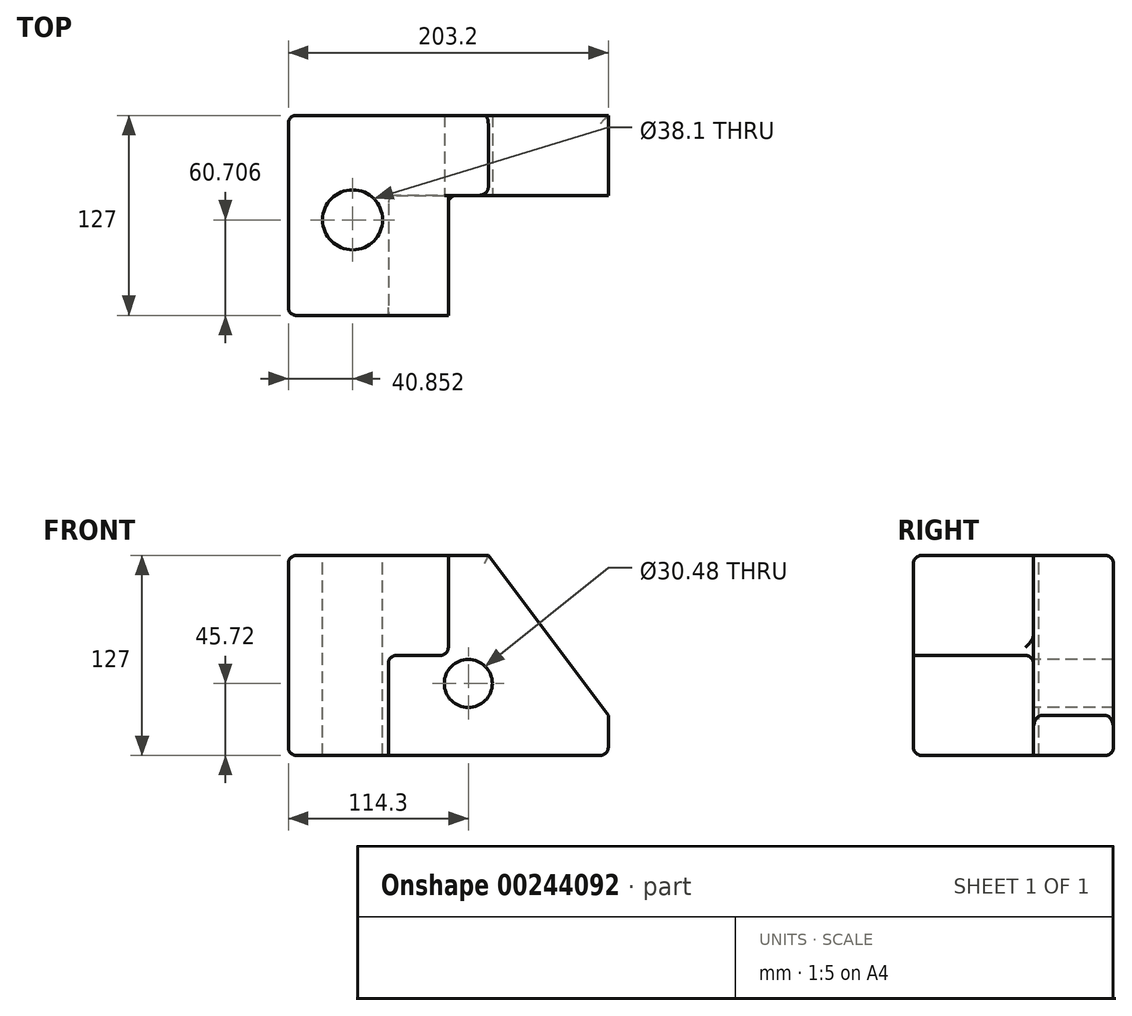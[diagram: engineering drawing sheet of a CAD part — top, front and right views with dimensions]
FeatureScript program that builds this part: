
annotation { "Feature Type Name" : "Feature", "Feature Type Description" : "" }
export const myFeature = defineFeature(function(context is Context, id is Id, definition is map)
    precondition{}
    {
        {
            var Q0;
            Q0=qCreatedBy(makeId("Front.planeOp"),FACE);
            var sketch = newSketch(context, id + "F0", { "sketchPlane" : qUnion([Q0])});
            skLineSegment(sketch, "E0.bottom", {"start": v(101.6, 63.5) * mm, "end": v(-101.6, 63.5) * mm});
            skLineSegment(sketch, "E0.top", {"start": v(101.6, -63.5) * mm, "end": v(-101.6, -63.5) * mm});
            skLineSegment(sketch, "E0.left", {"start": v(101.6, 63.5) * mm, "end": v(101.6, -63.5) * mm});
            skLineSegment(sketch, "E0.right", {"start": v(-101.6, 63.5) * mm, "end": v(-101.6, -63.5) * mm});
            skPoint(sketch, "E0.middle", {"position": v(0, 0) * mm});
            skLineSegment(sketch, "E1", {"start": v(-38.1, -63.5) * mm, "end": v(-38.1, 0) * mm});
            skLineSegment(sketch, "E2", {"start": v(-38.1, 0) * mm, "end": v(0, 0) * mm});
            skLineSegment(sketch, "E3", {"start": v(0, 0) * mm, "end": v(0, 63.5) * mm});
            skSolve(sketch);
        }
        {
            var Q0;
            {var subQ1=sQuery(id+"F0.wireOp",EDGE,"E0.left");Q0=makeQuery(id+"F0.imprint","IMPRINT",FACE,{"disambiguationData":[TD([[makeQuery(id+"F0.imprint","IMPRINT",EDGE,{"derivedFrom":subQ1}),-1.0]])]});}
            var Q1;
            {var subQ1=sQuery(id+"F0.wireOp",EDGE,"E0.right");Q1=makeQuery(id+"F0.imprint","IMPRINT",FACE,{"disambiguationData":[TD([[makeQuery(id+"F0.imprint","IMPRINT",EDGE,{"derivedFrom":subQ1}),1.0]])]});}
            extrude(context, id + "F1", {"entities" : qUnion([Q0, Q1]), "depth" : 127 * mm});
        }
        {
            var Q0;
            Q0=makeQuery(id+"F1.opExtrude","CAP_FACE",FACE,{"disambiguationData":[OSD([sQuery(id+"F0.wireOp",EDGE,"E0.bottom"),sQuery(id+"F0.wireOp",EDGE,"E0.top"),sQuery(id+"F0.wireOp",EDGE,"E0.left"),sQuery(id+"F0.wireOp",EDGE,"E0.right")])],"isStart":false});
            var sketch = newSketch(context, id + "F2", { "sketchPlane" : qUnion([Q0])});
            skLineSegment(sketch, "E4", {"start": v(-101.6, -63.5) * mm, "end": v(-38.1, -63.5) * mm});
            skLineSegment(sketch, "E5", {"start": v(-38.1, -63.5) * mm, "end": v(-38.1, 0) * mm});
            skLineSegment(sketch, "E6", {"start": v(-38.1, 0) * mm, "end": v(0, 0) * mm});
            skLineSegment(sketch, "E7", {"start": v(0, 0) * mm, "end": v(0, 63.5) * mm});
            skSolve(sketch);
        }
        {
            var Q0;
            {var subQ2=sQuery(id+"F2.wireOp",EDGE,"E5");Q0=makeQuery(id+"F2.imprint","IMPRINT",FACE,{"disambiguationData":[TD([[makeQuery(id+"F2.imprint","IMPRINT",EDGE,{"derivedFrom":subQ2}),-1.0]])]});}
            extrude(context, id + "F3", {"entities" : qUnion([Q0]), "operationType" : NewBodyOperationType.REMOVE, "oppositeDirection" : true, "depth" : 76.2 * mm});
        }
        {
            var Q0;
            Q0=makeQuery(id+"F1.opExtrude","SWEPT_EDGE",EDGE,{"disambiguationData":[OSD([sQuery(id+"F0.wireOp",EDGE,"E0.bottom"),sQuery(id+"F0.wireOp",EDGE,"E0.left")])]});
            chamfer(context, id + "F4", {"entities" : qUnion([Q0]), "chamferType" : ChamferType.TWO_OFFSETS, "width1" : 76.2 * mm, "oppositeDirection" : false, "width2" : 101.6 * mm, "tangentPropagation" : true});
        }
        {
            var Q0;
            {var subQ0=sQuery(id+"F0.wireOp",EDGE,"E0.left");var subQ1=sQuery(id+"F0.wireOp",EDGE,"E0.bottom");Q0=makeQuery(id+"F4.opChamfer","BLEND_EDGE",EDGE,{"blendedFrom":[makeQuery(id+"F1.opExtrude","SWEPT_EDGE",EDGE,{"disambiguationData":[OSD([subQ1,subQ0])]}),makeQuery(id+"F3.boolean.opBoolean","COPY",FACE,{"derivedFrom":makeQuery(id+"F3.opExtrude","CAP_FACE",FACE,{"disambiguationData":[OSD([subQ1,sQuery(id+"F0.wireOp",EDGE,"E0.top"),subQ0,sQuery(id+"F2.wireOp",EDGE,"E5"),sQuery(id+"F2.wireOp",EDGE,"E6"),sQuery(id+"F2.wireOp",EDGE,"E7")])],"isStart":false})})],"blendedInto":[makeQuery(id+"F3.boolean.opBoolean","COPY",FACE,{"derivedFrom":makeQuery(id+"F3.opExtrude","CAP_FACE",FACE,{"disambiguationData":[OSD([subQ1,sQuery(id+"F0.wireOp",EDGE,"E0.top"),subQ0,sQuery(id+"F2.wireOp",EDGE,"E5"),sQuery(id+"F2.wireOp",EDGE,"E6"),sQuery(id+"F2.wireOp",EDGE,"E7")])],"isStart":false})})]});}
            var Q1;
            {var subQ0=sQuery(id+"F0.wireOp",EDGE,"E0.left");var subQ1=sQuery(id+"F0.wireOp",EDGE,"E0.bottom");Q1=makeQuery(id+"F4.opChamfer","BLEND_EDGE",EDGE,{"blendedFrom":[makeQuery(id+"F1.opExtrude","SWEPT_EDGE",EDGE,{"disambiguationData":[OSD([subQ1,subQ0])]}),makeQuery(id+"F1.opExtrude","CAP_FACE",FACE,{"disambiguationData":[OSD([subQ1,sQuery(id+"F0.wireOp",EDGE,"E0.top"),subQ0,sQuery(id+"F0.wireOp",EDGE,"E0.right")])],"isStart":true})],"blendedInto":[makeQuery(id+"F1.opExtrude","CAP_FACE",FACE,{"disambiguationData":[OSD([subQ1,sQuery(id+"F0.wireOp",EDGE,"E0.top"),subQ0,sQuery(id+"F0.wireOp",EDGE,"E0.right")])],"isStart":true})]});}
            var Q2;
            Q2=makeQuery(id+"F3.boolean.opBoolean","COPY",EDGE,{"derivedFrom":makeQuery(id+"F3.opExtrude","CAP_EDGE",EDGE,{"disambiguationData":[OSD([sQuery(id+"F0.wireOp",EDGE,"E0.bottom")])],"isStart":false})});
            var Q3;
            Q3=makeQuery(id+"F3.boolean.opBoolean","COPY",EDGE,{"derivedFrom":makeQuery(id+"F3.opExtrude","SWEPT_EDGE",EDGE,{"disambiguationData":[OSD([sQuery(id+"F0.wireOp",EDGE,"E0.bottom"),sQuery(id+"F2.wireOp",EDGE,"E7")])]})});
            var Q4;
            Q4=makeQuery(id+"F1.opExtrude","CAP_EDGE",EDGE,{"disambiguationData":[OSD([sQuery(id+"F0.wireOp",EDGE,"E0.bottom")])],"isStart":false});
            var Q5;
            Q5=makeQuery(id+"F3.boolean.opBoolean","COPY",EDGE,{"derivedFrom":makeQuery(id+"F3.opExtrude","CAP_EDGE",EDGE,{"disambiguationData":[OSD([sQuery(id+"F2.wireOp",EDGE,"E7")])],"isStart":true})});
            var Q6;
            Q6=makeQuery(id+"F3.boolean.opBoolean","COPY",EDGE,{"derivedFrom":makeQuery(id+"F3.opExtrude","SWEPT_EDGE",EDGE,{"disambiguationData":[OSD([sQuery(id+"F2.wireOp",EDGE,"E6"),sQuery(id+"F2.wireOp",EDGE,"E7")])]})});
            var Q7;
            Q7=makeQuery(id+"F3.boolean.opBoolean","COPY",EDGE,{"derivedFrom":makeQuery(id+"F3.opExtrude","CAP_EDGE",EDGE,{"disambiguationData":[OSD([sQuery(id+"F0.wireOp",EDGE,"E0.top")])],"isStart":false})});
            var Q8;
            Q8=makeQuery(id+"F3.boolean.opBoolean","COPY",EDGE,{"derivedFrom":makeQuery(id+"F3.opExtrude","CAP_EDGE",EDGE,{"disambiguationData":[OSD([sQuery(id+"F0.wireOp",EDGE,"E0.left")])],"isStart":false})});
            var Q9;
            Q9=makeQuery(id+"F1.opExtrude","SWEPT_EDGE",EDGE,{"disambiguationData":[OSD([sQuery(id+"F0.wireOp",EDGE,"E0.top"),sQuery(id+"F0.wireOp",EDGE,"E0.left")])]});
            var Q10;
            Q10=makeQuery(id+"F1.opExtrude","CAP_EDGE",EDGE,{"disambiguationData":[OSD([sQuery(id+"F0.wireOp",EDGE,"E0.right")])],"isStart":false});
            var Q11;
            Q11=makeQuery(id+"F1.opExtrude","CAP_EDGE",EDGE,{"disambiguationData":[OSD([sQuery(id+"F0.wireOp",EDGE,"E0.top")])],"isStart":false});
            var Q12;
            Q12=makeQuery(id+"F1.opExtrude","CAP_EDGE",EDGE,{"disambiguationData":[OSD([sQuery(id+"F0.wireOp",EDGE,"E0.bottom")])],"isStart":true});
            var Q13;
            Q13=makeQuery(id+"F1.opExtrude","CAP_EDGE",EDGE,{"disambiguationData":[OSD([sQuery(id+"F0.wireOp",EDGE,"E0.right")])],"isStart":true});
            var Q14;
            Q14=makeQuery(id+"F1.opExtrude","CAP_EDGE",EDGE,{"disambiguationData":[OSD([sQuery(id+"F0.wireOp",EDGE,"E0.top")])],"isStart":true});
            var Q15;
            Q15=makeQuery(id+"F1.opExtrude","SWEPT_EDGE",EDGE,{"disambiguationData":[OSD([sQuery(id+"F0.wireOp",EDGE,"E0.top"),sQuery(id+"F0.wireOp",EDGE,"E0.right")])]});
            var Q16;
            Q16=makeQuery(id+"F3.boolean.opBoolean","COPY",EDGE,{"derivedFrom":makeQuery(id+"F3.opExtrude","SWEPT_EDGE",EDGE,{"disambiguationData":[OSD([sQuery(id+"F0.wireOp",EDGE,"E0.top"),sQuery(id+"F2.wireOp",EDGE,"E4"),sQuery(id+"F2.wireOp",EDGE,"E5")])]})});
            var Q17;
            Q17=makeQuery(id+"F1.opExtrude","SWEPT_EDGE",EDGE,{"disambiguationData":[OSD([sQuery(id+"F0.wireOp",EDGE,"E0.bottom"),sQuery(id+"F0.wireOp",EDGE,"E0.right")])]});
            var Q18;
            Q18=makeQuery(id+"F3.boolean.opBoolean","COPY",EDGE,{"derivedFrom":makeQuery(id+"F3.opExtrude","CAP_EDGE",EDGE,{"disambiguationData":[OSD([sQuery(id+"F2.wireOp",EDGE,"E5")])],"isStart":true})});
            var Q19;
            Q19=makeQuery(id+"F3.boolean.opBoolean","COPY",EDGE,{"derivedFrom":makeQuery(id+"F3.opExtrude","CAP_EDGE",EDGE,{"disambiguationData":[OSD([sQuery(id+"F2.wireOp",EDGE,"E6")])],"isStart":true})});
            var Q20;
            Q20=makeQuery(id+"F3.boolean.opBoolean","COPY",EDGE,{"derivedFrom":makeQuery(id+"F3.opExtrude","SWEPT_EDGE",EDGE,{"disambiguationData":[OSD([sQuery(id+"F2.wireOp",EDGE,"E5"),sQuery(id+"F2.wireOp",EDGE,"E6")])]})});
            var Q21;
            Q21=makeQuery(id+"F3.boolean.opBoolean","COPY",EDGE,{"derivedFrom":makeQuery(id+"F3.opExtrude","CAP_EDGE",EDGE,{"disambiguationData":[OSD([sQuery(id+"F2.wireOp",EDGE,"E6")])],"isStart":false})});
            var Q22;
            Q22=makeQuery(id+"F3.boolean.opBoolean","COPY",EDGE,{"derivedFrom":makeQuery(id+"F3.opExtrude","CAP_EDGE",EDGE,{"disambiguationData":[OSD([sQuery(id+"F2.wireOp",EDGE,"E5")])],"isStart":false})});
            fillet(context, id + "F5", {"entities" : qUnion([Q0, Q1, Q2, Q3, Q4, Q5, Q6, Q7, Q8, Q9, Q10, Q11, Q12, Q13, Q14, Q15, Q16, Q17, Q18, Q19, Q20, Q21, Q22]), "radius" : 5.08 * mm, "tangentPropagation" : true, "allowEdgeOverflow" : false});
        }
        {
            var Q0;
            Q0=makeQuery(id+"F3.boolean.opBoolean","COPY",FACE,{"derivedFrom":makeQuery(id+"F3.opExtrude","CAP_FACE",FACE,{"disambiguationData":[OSD([sQuery(id+"F0.wireOp",EDGE,"E0.bottom"),sQuery(id+"F0.wireOp",EDGE,"E0.top"),sQuery(id+"F0.wireOp",EDGE,"E0.left"),sQuery(id+"F2.wireOp",EDGE,"E5"),sQuery(id+"F2.wireOp",EDGE,"E6"),sQuery(id+"F2.wireOp",EDGE,"E7")])],"isStart":false})});
            var sketch = newSketch(context, id + "F6", { "sketchPlane" : qUnion([Q0])});
            skCircle(sketch, "E8", {"center": v(12.7, -17.78) * mm, "radius": 15.24 * mm});
            skSolve(sketch);
        }
        {
            var Q0;
            Q0=makeQuery(id+"F6.imprint","IMPRINT",FACE,{"disambiguationData":[TD([[makeQuery(id+"F6.imprint","IMPRINT",EDGE,{"derivedFrom":sQuery(id+"F6.wireOp",EDGE,"E8")}),1.0]])]});
            var Q1;
            Q1=makeQuery(id+"F1.opExtrude","CAP_FACE",FACE,{"disambiguationData":[OSD([sQuery(id+"F0.wireOp",EDGE,"E0.bottom"),sQuery(id+"F0.wireOp",EDGE,"E0.top"),sQuery(id+"F0.wireOp",EDGE,"E0.left"),sQuery(id+"F0.wireOp",EDGE,"E0.right")])],"isStart":true});
            extrude(context, id + "F7", {"entities" : qUnion([Q0]), "operationType" : NewBodyOperationType.REMOVE, "endBound" : BoundingType.UP_TO_SURFACE, "oppositeDirection" : true, "endBoundEntityFace" : qUnion([Q1]), "depth" : 25.4 * mm});
        }
        {
            var Q0;
            Q0=makeQuery(id+"F1.opExtrude","SWEPT_FACE",FACE,{"disambiguationData":[OSD([sQuery(id+"F0.wireOp",EDGE,"E0.bottom")])]});
            var sketch = newSketch(context, id + "F8", { "sketchPlane" : qUnion([Q0])});
            skCircle(sketch, "E9", {"center": v(-60.75, -66.3) * mm, "radius": 19.05 * mm});
            skSolve(sketch);
        }
        {
            var Q0;
            Q0=makeQuery(id+"F8.imprint","IMPRINT",FACE,{"disambiguationData":[TD([[makeQuery(id+"F8.imprint","IMPRINT",EDGE,{"derivedFrom":sQuery(id+"F8.wireOp",EDGE,"E9")}),1.0]])]});
            var Q1;
            Q1=makeQuery(id+"F1.opExtrude","SWEPT_FACE",FACE,{"disambiguationData":[OSD([sQuery(id+"F0.wireOp",EDGE,"E0.top")])]});
            extrude(context, id + "F9", {"entities" : qUnion([Q0]), "operationType" : NewBodyOperationType.REMOVE, "endBound" : BoundingType.UP_TO_SURFACE, "oppositeDirection" : true, "endBoundEntityFace" : qUnion([Q1]), "depth" : 25.4 * mm});
        }
    });
